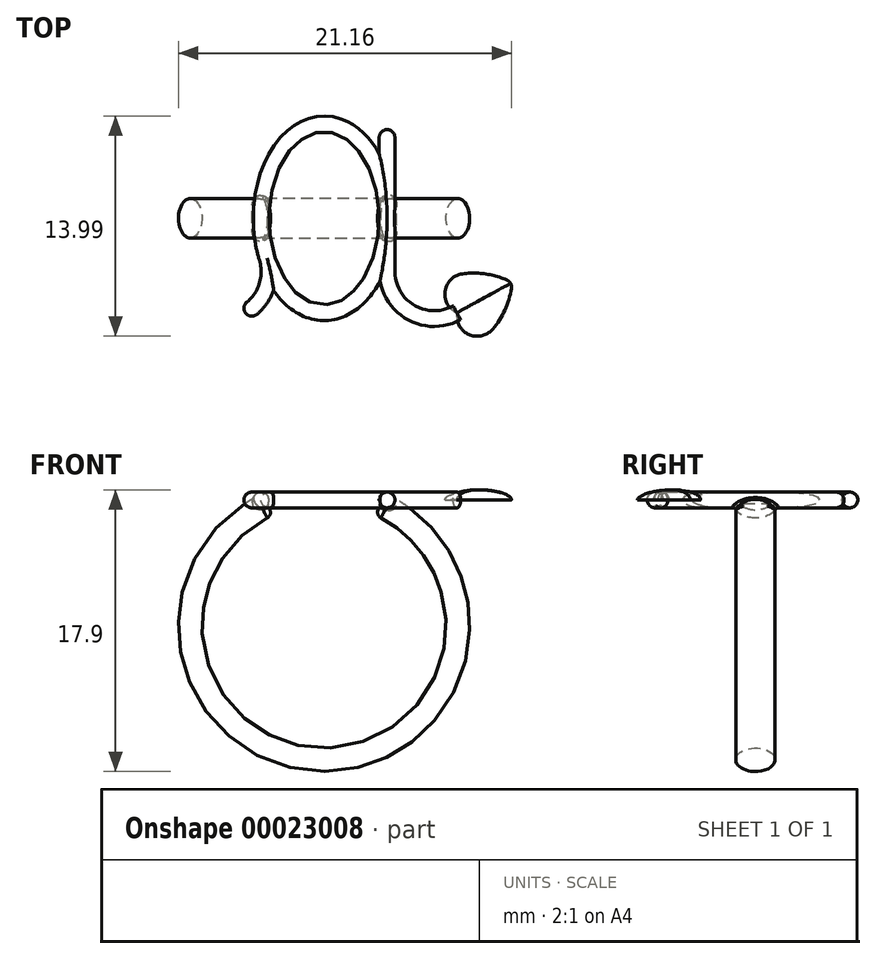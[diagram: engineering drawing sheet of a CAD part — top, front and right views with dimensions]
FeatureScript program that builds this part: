
annotation { "Feature Type Name" : "Feature", "Feature Type Description" : "" }
export const myFeature = defineFeature(function(context is Context, id is Id, definition is map)
    precondition{}
    {
        {
            var Q0;
            Q0=qCreatedBy(makeId("Right.planeOp"),FACE);
            var sketch = newSketch(context, id + "F0", { "sketchPlane" : qUnion([Q0])});
            skEllipse(sketch, "E0", {"center": v(0, -8.5) * mm, "majorRadius": 1.25 * mm, "minorRadius": 0.75 * mm, "majorAxis": v(1, 0)});
            skLineSegment(sketch, "E1", {"start": v(-8.37, 0) * mm, "end": v(10.93, 0) * mm, "construction": true});
            skSolve(sketch);
        }
        {
            var Q0;
            Q0=makeQuery(id+"F0.imprint","IMPRINT",FACE,{"disambiguationData":[TD([[makeQuery(id+"F0.imprint","IMPRINT",EDGE,{"derivedFrom":sQuery(id+"F0.wireOp",EDGE,"E0")}),1.0]])]});
            var Q1;
            Q1=sQuery(id+"F0.wireOp",EDGE,"E1");
            revolve(context, id + "F1", {"entities" : qUnion([Q0]), "axis" : qUnion([Q1]), "revolveType" : RevolveType.TWO_DIRECTIONS, "angle" : 155 * degree, "angleBack" : 205 * degree});
        }
        {
            var Q0;
            Q0=qCreatedBy(makeId("Top.planeOp"),FACE);
            cPlane(context, id + "F2", {"entities" : qUnion([Q0]), "cplaneType" : CPlaneType.OFFSET, "offset" : 8 * mm, "width" : 150 * mm, "height" : 150 * mm});
        }
        {
            var Q0;
            Q0=qCreatedBy(id+"F2.planeOp",FACE);
            var sketch = newSketch(context, id + "F3", { "sketchPlane" : qUnion([Q0])});
            skEllipse(sketch, "E2", {"center": v(0, 0) * mm, "majorRadius": 6 * mm, "minorRadius": 4 * mm, "majorAxis": v(0, 1)});
            skLineSegment(sketch, "E3", {"start": v(4, 5.63) * mm, "end": v(4, -3.37) * mm});
            skArc(sketch, "E4", {"start": v(4, -3.37) * mm, "mid": v(5.47, -5.95) * mm, "end": v(8.44, -6) * mm});
            skLineSegment(sketch, "E5", {"start": v(-7.83, -6) * mm, "end": v(11.12, -6) * mm, "construction": true});
            skArc(sketch, "E6", {"start": v(-5, -6) * mm, "mid": v(-3.7, -4.5) * mm, "end": v(-3.63, -2.52) * mm});
            skSolve(sketch);
        }
        {
            var Q0;
            Q0=sQuery(id+"F3.wireOp",VERTEX,"E3.start");
            var Q1;
            Q1=sQuery(id+"F3.wireOp",EDGE,"E3");
            cPlane(context, id + "F4", {"entities" : qUnion([Q0, Q1]), "cplaneType" : CPlaneType.LINE_POINT, "offset" : 150 * mm, "width" : 150 * mm, "height" : 150 * mm});
        }
        {
            var Q0;
            Q0=qCreatedBy(id+"F4.planeOp",FACE);
            var sketch = newSketch(context, id + "F5", { "sketchPlane" : qUnion([Q0])});
            skCircle(sketch, "E7", {"center": v(4, 8) * mm, "radius": 0.5 * mm});
            skSolve(sketch);
        }
        {
            var Q0;
            Q0=makeQuery(id+"F5.imprint","IMPRINT",FACE,{"disambiguationData":[TD([[makeQuery(id+"F5.imprint","IMPRINT",EDGE,{"derivedFrom":sQuery(id+"F5.wireOp",EDGE,"E7")}),1.0]])]});
            var Q1;
            Q1=sQuery(id+"F3.wireOp",EDGE,"E3");
            var Q2;
            Q2=sQuery(id+"F3.wireOp",EDGE,"E4");
            sweep(context, id + "F6", {"operationType" : NewBodyOperationType.ADD, "profiles" : qUnion([Q0]), "path" : qUnion([Q1, Q2])});
        }
        {
            var Q0;
            Q0=qCreatedBy(makeId("Right.planeOp"),FACE);
            var sketch = newSketch(context, id + "F7", { "sketchPlane" : qUnion([Q0])});
            skCircle(sketch, "E8", {"center": v(6, 8) * mm, "radius": 0.5 * mm});
            skLineSegment(sketch, "E9.0", {"start": v(-6, 8) * mm, "end": v(6, 8) * mm});
            skSolve(sketch);
        }
        {
            var Q0;
            Q0=makeQuery(id+"F7.imprint","IMPRINT",FACE,{"disambiguationData":[TD([[makeQuery(id+"F7.imprint","IMPRINT",EDGE,{"derivedFrom":sQuery(id+"F7.wireOp",EDGE,"E8")}),1.0]])]});
            var Q1;
            Q1=sQuery(id+"F3.wireOp",EDGE,"E2");
            sweep(context, id + "F8", {"operationType" : NewBodyOperationType.ADD, "profiles" : qUnion([Q0]), "path" : qUnion([Q1])});
        }
        {
            var Q0;
            Q0=sQuery(id+"F3.wireOp",VERTEX,"E6.start");
            var Q1;
            Q1=sQuery(id+"F3.wireOp",EDGE,"E6");
            cPlane(context, id + "F9", {"entities" : qUnion([Q0, Q1]), "cplaneType" : CPlaneType.CURVE_POINT, "offset" : 150 * mm, "width" : 150 * mm, "height" : 150 * mm});
        }
        {
            var Q0;
            Q0=qCreatedBy(id+"F9.planeOp",FACE);
            var sketch = newSketch(context, id + "F10", { "sketchPlane" : qUnion([Q0])});
            skCircle(sketch, "E10", {"center": v(-2.7, 8) * mm, "radius": 0.5 * mm});
            skSolve(sketch);
        }
        {
            var Q0;
            Q0=makeQuery(id+"F10.imprint","IMPRINT",FACE,{"disambiguationData":[TD([[makeQuery(id+"F10.imprint","IMPRINT",EDGE,{"derivedFrom":sQuery(id+"F10.wireOp",EDGE,"E10")}),1.0]])]});
            var Q1;
            Q1=sQuery(id+"F3.wireOp",EDGE,"E6");
            sweep(context, id + "F11", {"operationType" : NewBodyOperationType.ADD, "profiles" : qUnion([Q0]), "path" : qUnion([Q1])});
        }
        {
            var Q0;
            Q0=makeQuery(id+"F1.opRevolve","CAP_EDGE",EDGE,{"disambiguationData":[OSD([sQuery(id+"F0.wireOp",EDGE,"E0")])],"isStart":false});
            var Q1;
            Q1=makeQuery(id+"F1.opRevolve","CAP_EDGE",EDGE,{"disambiguationData":[OSD([sQuery(id+"F0.wireOp",EDGE,"E0")])],"isStart":true});
            fillet(context, id + "F12", {"entities" : qUnion([Q0, Q1]), "radius" : .4 * mm, "tangentPropagation" : true, "allowEdgeOverflow" : false});
        }
        {
            var Q0;
            Q0=makeQuery(id+"F6.opSweep","CAP_EDGE",EDGE,{"disambiguationData":[OSD([sQuery(id+"F3.wireOp",VERTEX,"E3.start"),sQuery(id+"F5.wireOp",EDGE,"E7")])],"isStart":true});
            var Q1;
            Q1=makeQuery(id+"F11.opSweep","CAP_EDGE",EDGE,{"disambiguationData":[OSD([sQuery(id+"F3.wireOp",VERTEX,"E6.start"),sQuery(id+"F10.wireOp",EDGE,"E10")])],"isStart":true});
            fillet(context, id + "F13", {"entities" : qUnion([Q0, Q1]), "radius" : .5 * mm, "tangentPropagation" : true, "allowEdgeOverflow" : false});
        }
        {
            var Q0;
            Q0=makeQuery(id+"F12.opFillet","BLEND_EDGE",EDGE,{"disambiguationData":[OD(0.0)],"blendedFrom":[makeQuery(id+"F1.opRevolve","CAP_EDGE",EDGE,{"disambiguationData":[OSD([sQuery(id+"F0.wireOp",EDGE,"E0")])],"isStart":true}),makeQuery(id+"F8.opSweep","SWEPT_FACE",FACE,{"disambiguationData":[OSD([sQuery(id+"F3.wireOp",EDGE,"E2"),sQuery(id+"F7.wireOp",EDGE,"E8")])]})],"blendedInto":[makeQuery(id+"F8.opSweep","SWEPT_FACE",FACE,{"disambiguationData":[OSD([sQuery(id+"F3.wireOp",EDGE,"E2"),sQuery(id+"F7.wireOp",EDGE,"E8")])]})]});
            var Q1;
            Q1=makeQuery(id+"F8.boolean.opBoolean","INTERSECT",EDGE,{"derivedFrom":[makeQuery(id+"F1.opRevolve","CAP_FACE",FACE,{"disambiguationData":[OSD([sQuery(id+"F0.wireOp",EDGE,"E0")])],"isStart":true}),makeQuery(id+"F8.opSweep","SWEPT_FACE",FACE,{"disambiguationData":[OSD([sQuery(id+"F3.wireOp",EDGE,"E2"),sQuery(id+"F7.wireOp",EDGE,"E8")])]})]});
            var Q2;
            Q2=makeQuery(id+"F6.boolean.opBoolean","INTERSECT",EDGE,{"derivedFrom":[makeQuery(id+"F1.opRevolve","SWEPT_FACE",FACE,{"disambiguationData":[OSD([sQuery(id+"F0.wireOp",EDGE,"E0")])]}),makeQuery(id+"F6.opSweep","SWEPT_FACE",FACE,{"disambiguationData":[OSD([sQuery(id+"F3.wireOp",EDGE,"E3"),sQuery(id+"F5.wireOp",EDGE,"E7")])]})]});
            var Q3;
            Q3=makeQuery(id+"F12.opFillet","BLEND_EDGE",EDGE,{"disambiguationData":[OD(1.0)],"blendedFrom":[makeQuery(id+"F1.opRevolve","CAP_EDGE",EDGE,{"disambiguationData":[OSD([sQuery(id+"F0.wireOp",EDGE,"E0")])],"isStart":true}),makeQuery(id+"F8.opSweep","SWEPT_FACE",FACE,{"disambiguationData":[OSD([sQuery(id+"F3.wireOp",EDGE,"E2"),sQuery(id+"F7.wireOp",EDGE,"E8")])]})],"blendedInto":[makeQuery(id+"F8.opSweep","SWEPT_FACE",FACE,{"disambiguationData":[OSD([sQuery(id+"F3.wireOp",EDGE,"E2"),sQuery(id+"F7.wireOp",EDGE,"E8")])]})]});
            var Q4;
            Q4=makeQuery(id+"F12.opFillet","BLEND_EDGE",EDGE,{"disambiguationData":[OD(1.0)],"blendedFrom":[makeQuery(id+"F1.opRevolve","CAP_EDGE",EDGE,{"disambiguationData":[OSD([sQuery(id+"F0.wireOp",EDGE,"E0")])],"isStart":false}),makeQuery(id+"F8.opSweep","SWEPT_FACE",FACE,{"disambiguationData":[OSD([sQuery(id+"F3.wireOp",EDGE,"E2"),sQuery(id+"F7.wireOp",EDGE,"E8")])]})],"blendedInto":[makeQuery(id+"F8.opSweep","SWEPT_FACE",FACE,{"disambiguationData":[OSD([sQuery(id+"F3.wireOp",EDGE,"E2"),sQuery(id+"F7.wireOp",EDGE,"E8")])]})]});
            var Q5;
            {var subQ0=sQuery(id+"F0.wireOp",EDGE,"E0");Q5=makeQuery(id+"F12.opFillet","BLEND_EDGE",EDGE,{"blendedFrom":[makeQuery(id+"F1.opRevolve","CAP_EDGE",EDGE,{"disambiguationData":[OSD([subQ0])],"isStart":false}),makeQuery(id+"F1.opRevolve","CAP_FACE",FACE,{"disambiguationData":[OSD([subQ0])],"isStart":false})],"blendedInto":[makeQuery(id+"F1.opRevolve","CAP_FACE",FACE,{"disambiguationData":[OSD([subQ0])],"isStart":false})]});}
            var Q6;
            Q6=makeQuery(id+"F8.boolean.opBoolean","INTERSECT",EDGE,{"disambiguationData":[OD(2.0)],"derivedFrom":[makeQuery(id+"F1.opRevolve","SWEPT_FACE",FACE,{"disambiguationData":[OSD([sQuery(id+"F0.wireOp",EDGE,"E0")])]}),makeQuery(id+"F8.opSweep","SWEPT_FACE",FACE,{"disambiguationData":[OSD([sQuery(id+"F3.wireOp",EDGE,"E2"),sQuery(id+"F7.wireOp",EDGE,"E8")])]})]});
            var Q7;
            Q7=makeQuery(id+"F12.opFillet","BLEND_EDGE",EDGE,{"disambiguationData":[OD(0.0)],"blendedFrom":[makeQuery(id+"F1.opRevolve","CAP_EDGE",EDGE,{"disambiguationData":[OSD([sQuery(id+"F0.wireOp",EDGE,"E0")])],"isStart":false}),makeQuery(id+"F8.opSweep","SWEPT_FACE",FACE,{"disambiguationData":[OSD([sQuery(id+"F3.wireOp",EDGE,"E2"),sQuery(id+"F7.wireOp",EDGE,"E8")])]})],"blendedInto":[makeQuery(id+"F8.opSweep","SWEPT_FACE",FACE,{"disambiguationData":[OSD([sQuery(id+"F3.wireOp",EDGE,"E2"),sQuery(id+"F7.wireOp",EDGE,"E8")])]})]});
            fillet(context, id + "F14", {"entities" : qUnion([Q0, Q1, Q2, Q3, Q4, Q5, Q6, Q7]), "radius" : .2 * mm, "tangentPropagation" : true, "allowEdgeOverflow" : false});
        }
        {
            var Q0;
            Q0=makeQuery(id+"F6.opSweep","CAP_FACE",FACE,{"disambiguationData":[OSD([sQuery(id+"F3.wireOp",VERTEX,"E4.end"),sQuery(id+"F5.wireOp",EDGE,"E7")])],"isStart":false});
            cPlane(context, id + "F15", {"entities" : qUnion([Q0]), "cplaneType" : CPlaneType.OFFSET, "offset" : 0 * mm, "width" : 150 * mm, "height" : 150 * mm});
        }
        {
            var Q0;
            Q0=qCreatedBy(id+"F15.planeOp",FACE);
            cPlane(context, id + "F16", {"entities" : qUnion([Q0]), "cplaneType" : CPlaneType.OFFSET, "offset" : 1.5 * mm, "width" : 150 * mm, "height" : 150 * mm});
        }
        {
            var Q0;
            Q0=qCreatedBy(id+"F16.planeOp",FACE);
            cPlane(context, id + "F17", {"entities" : qUnion([Q0]), "cplaneType" : CPlaneType.OFFSET, "offset" : 2.5 * mm, "width" : 150 * mm, "height" : 150 * mm});
        }
        {
            var Q0;
            Q0=qCreatedBy(id+"F15.planeOp",FACE);
            var sketch = newSketch(context, id + "F18", { "sketchPlane" : qUnion([Q0])});
            skPoint(sketch, "E11", {"position": v(-9.32, 8) * mm});
            skCircle(sketch, "E12.0.0", {"center": v(-9.32, 8) * mm, "radius": 0.5 * mm});
            skSolve(sketch);
        }
        {
            var Q0;
            Q0=qCreatedBy(id+"F16.planeOp",FACE);
            var sketch = newSketch(context, id + "F19", { "sketchPlane" : qUnion([Q0])});
            skEllipse(sketch, "E13", {"center": v(-9.32, 8) * mm, "majorRadius": 2 * mm, "minorRadius": 0.65 * mm, "majorAxis": v(1, 0)});
            skLineSegment(sketch, "E14", {"start": v(-7.32, 9.11) * mm, "end": v(-7.32, 6.5) * mm, "construction": true});
            skLineSegment(sketch, "E15", {"start": v(-11.32, 9.41) * mm, "end": v(-11.32, 7.2) * mm, "construction": true});
            skSolve(sketch);
        }
        {
            var Q0;
            Q0=qCreatedBy(id+"F17.planeOp",FACE);
            var sketch = newSketch(context, id + "F20", { "sketchPlane" : qUnion([Q0])});
            skPoint(sketch, "E16", {"position": v(-9.32, 8) * mm});
            skSolve(sketch);
        }
        {
            var Q0;
            Q0=qCreatedBy(id+"F2.planeOp",FACE);
            var sketch = newSketch(context, id + "F21", { "sketchPlane" : qUnion([Q0])});
            skArc(sketch, "E17", {"start": v(8.8, -3.53) * mm, "mid": v(7.68, -4.63) * mm, "end": v(8.44, -6) * mm, "construction": true});
            skArc(sketch, "E18", {"start": v(8.8, -3.53) * mm, "mid": v(10.23, -3.53) * mm, "end": v(11.6, -3.92) * mm, "construction": true});
            skPoint(sketch, "E19", {"position": v(8.8, -3.53) * mm});
            skLineSegment(sketch, "E20", {"start": v(8.44, -6) * mm, "end": v(11.95, -4.08) * mm, "construction": true});
            skArc(sketch, "E21.MirrorCS", {"start": v(10.72, -7.03) * mm, "mid": v(11.49, -5.83) * mm, "end": v(11.9, -4.45) * mm});
            skArc(sketch, "E22.MirrorCS", {"start": v(10.72, -7.03) * mm, "mid": v(9.19, -7.38) * mm, "end": v(8.44, -6) * mm});
            skPoint(sketch, "E23.visualSharp", {"position": v(11.95, -4.08) * mm});
            skArc(sketch, "E23.filletArc", {"start": v(11.9, -4.45) * mm, "mid": v(11.9, -4.29) * mm, "end": v(11.85, -4.13) * mm});
            skArc(sketch, "E24", {"start": v(11.85, -4.13) * mm, "mid": v(11.75, -4) * mm, "end": v(11.6, -3.92) * mm, "construction": true});
            skSolve(sketch);
        }
        {
            var Q0;
            Q0=sQuery(id+"F21.wireOp",EDGE,"E20");
            cPlane(context, id + "F22", {"entities" : qUnion([Q0]), "cplaneType" : CPlaneType.LINE_ANGLE, "offset" : 150 * mm, "angle" : 0 * degree, "width" : 150 * mm, "height" : 150 * mm});
        }
        {
            var Q0;
            Q0=qCreatedBy(id+"F22.planeOp",FACE);
            var sketch = newSketch(context, id + "F23", { "sketchPlane" : qUnion([Q0])});
            skLineSegment(sketch, "E25", {"start": v(-6.02, 8) * mm, "end": v(-6.02, 8.65) * mm});
            skLineSegment(sketch, "E26", {"start": v(-6.02, 8) * mm, "end": v(-8.4, 8) * mm});
            skEllipticalArc(sketch, "E27", {});
            const initialGuessF23  = {"E27": [-0.006023315396989856, 0.008, -1, 0, 0.0023850018281689226, 0.00065, 4.71238898038469, 0]};
            skSetInitialGuess(sketch, initialGuessF23);
            skSolve(sketch);
        }
        {
            var Q0;
            Q0=qCreatedBy(id+"F16.planeOp",FACE);
            var sketch = newSketch(context, id + "F24", { "sketchPlane" : qUnion([Q0])});
            skLineSegment(sketch, "E28.0", {"start": v(-9.32, 8) * mm, "end": v(-9.32, 8.65) * mm});
            skLineSegment(sketch, "E29", {"start": v(-9.32, 8) * mm, "end": v(-11.32, 8) * mm});
            skEllipticalArc(sketch, "E30.0", {});
            const initialGuessF24  = {"E30.0": [-0.009315497004728895, 0.008, 1, 0, 0.002, 0.00065, 1.5707963267948974, 3.141592653589793]};
            skSetInitialGuess(sketch, initialGuessF24);
            skSolve(sketch);
        }
        {
            var Q0;
            Q0=qCreatedBy(id+"F22.planeOp",FACE);
            var sketch = newSketch(context, id + "F25", { "sketchPlane" : qUnion([Q0])});
            skLineSegment(sketch, "E31.0", {"start": v(-4.52, 8) * mm, "end": v(-6.02, 8) * mm});
            skLineSegment(sketch, "E31.1", {"start": v(-6.02, 8) * mm, "end": v(-6.02, 8.65) * mm});
            skPoint(sketch, "E32.orphan", {"position": v(-8.52, 8) * mm});
            skEllipticalArc(sketch, "E33", {});
            const initialGuessF25  = {"E33": [-0.006023315396989857, 0.008, 1, 0, 0.0015, 0.00065, 0, 1.5707963267948972]};
            skSetInitialGuess(sketch, initialGuessF25);
            skSolve(sketch);
        }
        {
            var Q0;
            Q0 = qSketchRegion(id + "F23", true);
            var Q1;
            Q1 = qSketchRegion(id + "F24", true);
            var Q2;
            Q2 = qSketchRegion(id + "F25", true);
            var Q3;
            Q3 = qConstructionFilter(qBodyType(qCreatedBy(id + "F21" ,EDGE), BodyType.WIRE), ConstructionObject.NO);
            loft(context, id + "F26", {"addGuides" : true, "sheetProfilesArray" : [{ "sheetProfileEntities" : qUnion([Q0]) }, { "sheetProfileEntities" : qUnion([Q1]) }, { "sheetProfileEntities" : qUnion([Q2]) }], "guidesArray" : [{ "guideEntities" : qUnion([Q3]), "guideDerivativeType" : LoftGuideDerivativeType.DEFAULT, "guideDerivativeMagnitude" : 1 }]});
        }
        {
            var Q0;
            Q0=makeQuery(id+"F26.opLoft","SWEPT_BODY",BODY,{"disambiguationData":[OSD([sQuery(id+"F21.wireOp",EDGE,"E22.MirrorCS"),makeQuery(id+"F23.imprint","IMPRINT",FACE,{"disambiguationData":[TD([[makeQuery(id+"F23.imprint","IMPRINT",EDGE,{"derivedFrom":sQuery(id+"F23.wireOp",EDGE,"E25")}),1.0]])]}),sQuery(id+"F24.wireOp",EDGE,"E28.0"),makeQuery(id+"F25.imprint","IMPRINT",FACE,{"disambiguationData":[TD([[makeQuery(id+"F25.imprint","IMPRINT",EDGE,{"derivedFrom":sQuery(id+"F25.wireOp",EDGE,"E31.0")}),-1.0]])]})])]});
            var Q1;
            Q1=qCreatedBy(id+"F22.planeOp",FACE);
            mirror(context, id + "F27", {"entities" : qUnion([Q0]), "mirrorPlane" : qUnion([Q1])});
        }
    });
